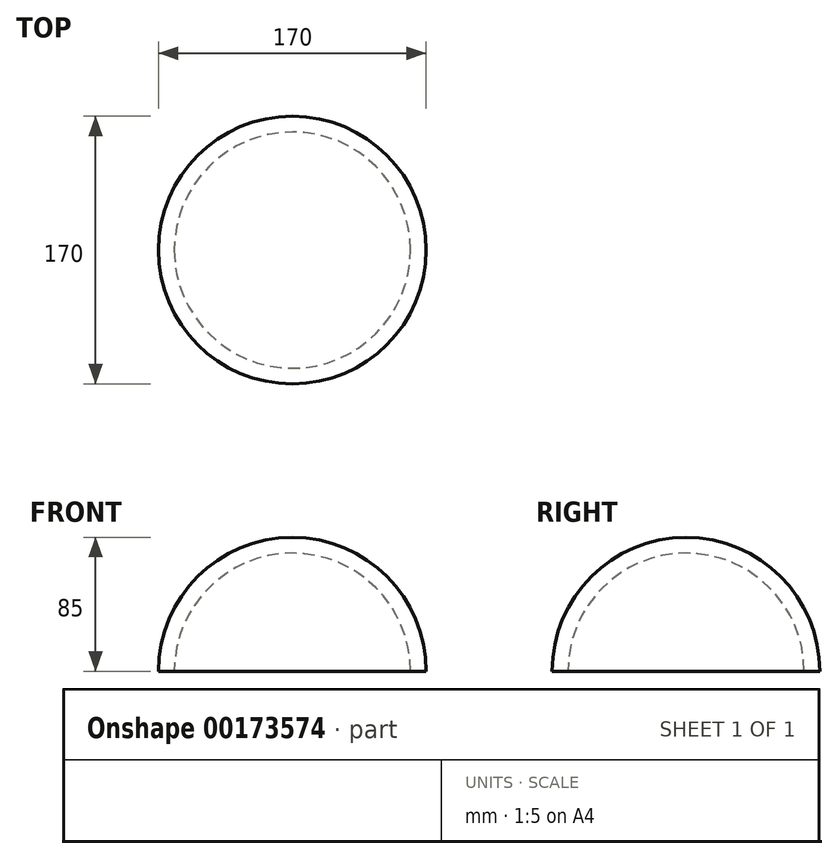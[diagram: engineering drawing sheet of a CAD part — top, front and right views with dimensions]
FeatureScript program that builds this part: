
annotation { "Feature Type Name" : "Feature", "Feature Type Description" : "" }
export const myFeature = defineFeature(function(context is Context, id is Id, definition is map)
    precondition{}
    {
        {
            var Q0;
            Q0=qCreatedBy(makeId("Top.planeOp"),FACE);
            var sketch = newSketch(context, id + "F0", { "sketchPlane" : qUnion([Q0])});
            skArc(sketch, "E0", {"start": v(-59.44, 35.6) * mm, "mid": v(25.56, -49.4) * mm, "end": v(110.56, 35.6) * mm});
            skArc(sketch, "E1", {"start": v(-49.44, 35.6) * mm, "mid": v(25.56, -39.4) * mm, "end": v(100.56, 35.6) * mm});
            skLineSegment(sketch, "E2", {"start": v(-49.44, 35.6) * mm, "end": v(-59.44, 35.6) * mm});
            skLineSegment(sketch, "E3", {"start": v(100.56, 35.6) * mm, "end": v(110.56, 35.6) * mm});
            skSolve(sketch);
        }
        {
            var Q0;
            Q0 = qSketchRegion(id + "F0", true);
            var Q1;
            Q1=sQuery(id+"F0.wireOp",EDGE,"E2");
            revolve(context, id + "F1", {"entities" : qUnion([Q0]), "axis" : qUnion([Q1]), "revolveType" : RevolveType.ONE_DIRECTION, "angle" : 180 * degree});
        }
    });
